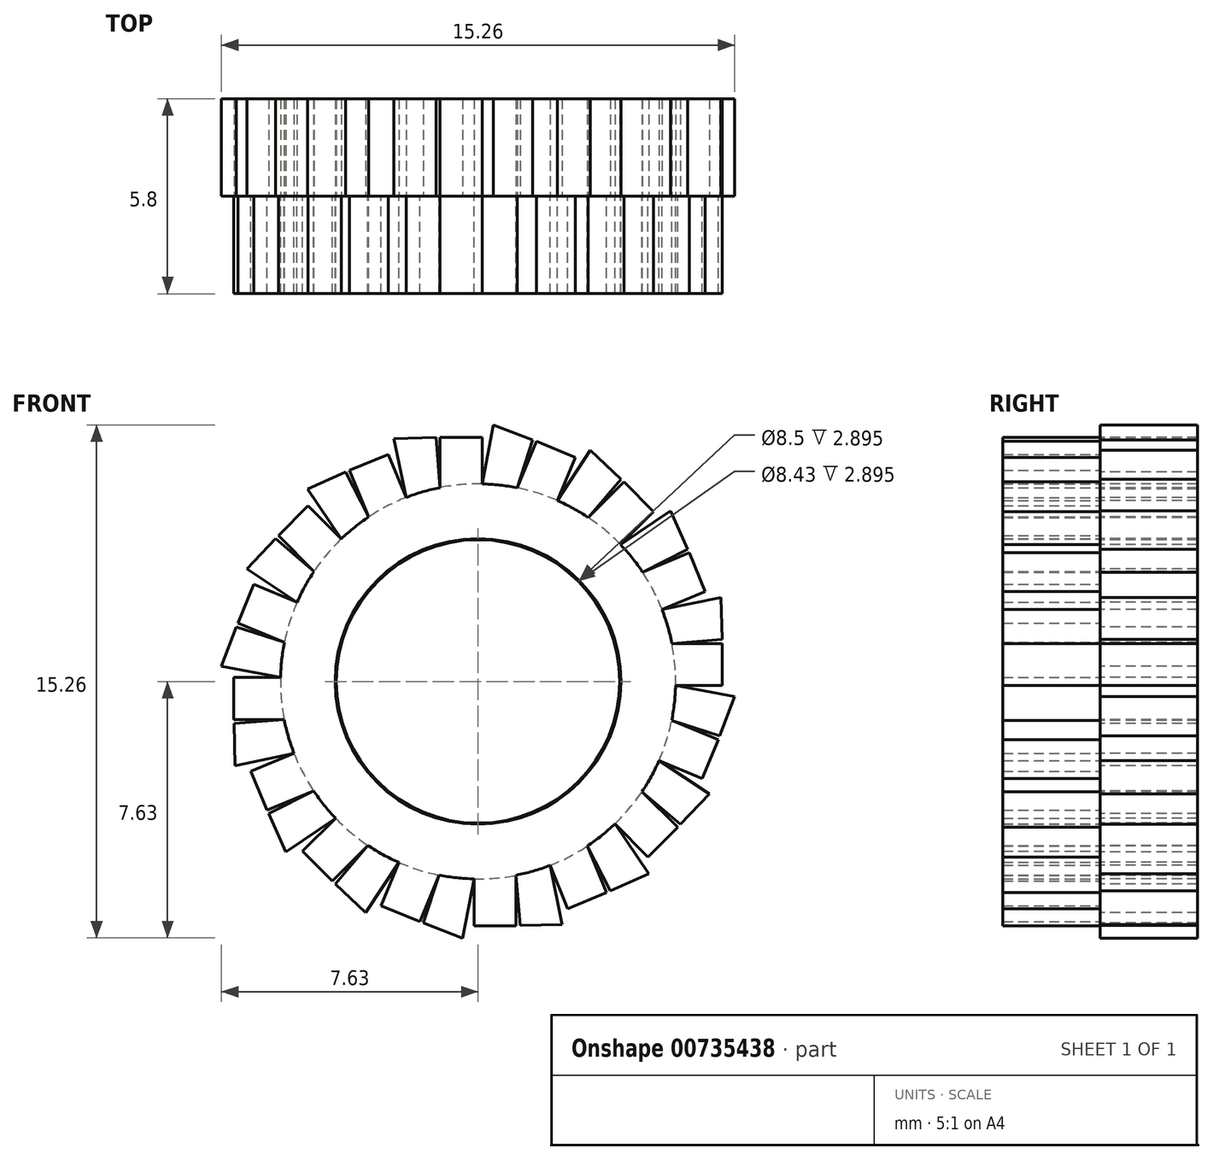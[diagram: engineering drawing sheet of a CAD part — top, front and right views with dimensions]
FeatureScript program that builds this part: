
annotation { "Feature Type Name" : "Feature", "Feature Type Description" : "" }
export const myFeature = defineFeature(function(context is Context, id is Id, definition is map)
    precondition{}
    {
        {
            var Q0;
            Q0=qCreatedBy(makeId("Front.planeOp"),FACE);
            var sketch = newSketch(context, id + "F0", { "sketchPlane" : qUnion([Q0])});
            skCircle(sketch, "E0", {"center": v(0, 0) * mm, "radius": 4.25 * mm});
            skCircle(sketch, "E1", {"center": v(0, 0) * mm, "radius": 5.88 * mm});
            skLineSegment(sketch, "E2", {"start": v(-1.13, 5.77) * mm, "end": v(-1.13, 7.27) * mm});
            skLineSegment(sketch, "E3", {"start": v(-1.13, 7.27) * mm, "end": v(0.12, 7.27) * mm});
            skLineSegment(sketch, "E4", {"start": v(0.12, 7.27) * mm, "end": v(0.12, 5.87) * mm});
            skLineSegment(sketch, "E5.1.0", {"start": v(-3.25, 4.9) * mm, "end": v(-3.83, 6.28) * mm});
            skLineSegment(sketch, "E5.1.1", {"start": v(-3.83, 6.28) * mm, "end": v(-2.67, 6.76) * mm});
            skLineSegment(sketch, "E5.1.2", {"start": v(-2.67, 6.76) * mm, "end": v(-2.14, 5.47) * mm});
            skLineSegment(sketch, "E5.2.0", {"start": v(-4.88, 3.28) * mm, "end": v(-5.94, 4.34) * mm});
            skLineSegment(sketch, "E5.2.1", {"start": v(-5.94, 4.34) * mm, "end": v(-5.05, 5.22) * mm});
            skLineSegment(sketch, "E5.2.2", {"start": v(-5.05, 5.22) * mm, "end": v(-4.07, 4.24) * mm});
            skLineSegment(sketch, "E5.3.0", {"start": v(-5.76, 1.16) * mm, "end": v(-7.14, 1.73) * mm});
            skLineSegment(sketch, "E5.3.1", {"start": v(-7.14, 1.73) * mm, "end": v(-6.67, 2.89) * mm});
            skLineSegment(sketch, "E5.3.2", {"start": v(-6.67, 2.89) * mm, "end": v(-5.38, 2.36) * mm});
            skLineSegment(sketch, "E5.4.0", {"start": v(-5.77, -1.13) * mm, "end": v(-7.27, -1.13) * mm});
            skLineSegment(sketch, "E5.4.1", {"start": v(-7.27, -1.13) * mm, "end": v(-7.27, 0.12) * mm});
            skLineSegment(sketch, "E5.4.2", {"start": v(-7.27, 0.12) * mm, "end": v(-5.87, 0.12) * mm});
            skLineSegment(sketch, "E5.5.0", {"start": v(-4.9, -3.25) * mm, "end": v(-6.28, -3.83) * mm});
            skLineSegment(sketch, "E5.5.1", {"start": v(-6.28, -3.83) * mm, "end": v(-6.76, -2.67) * mm});
            skLineSegment(sketch, "E5.5.2", {"start": v(-6.76, -2.67) * mm, "end": v(-5.47, -2.14) * mm});
            skLineSegment(sketch, "E5.6.0", {"start": v(-3.28, -4.88) * mm, "end": v(-4.34, -5.94) * mm});
            skLineSegment(sketch, "E5.6.1", {"start": v(-4.34, -5.94) * mm, "end": v(-5.22, -5.05) * mm});
            skLineSegment(sketch, "E5.6.2", {"start": v(-5.22, -5.05) * mm, "end": v(-4.24, -4.07) * mm});
            skLineSegment(sketch, "E5.7.0", {"start": v(-1.16, -5.76) * mm, "end": v(-1.73, -7.14) * mm});
            skLineSegment(sketch, "E5.7.1", {"start": v(-1.73, -7.14) * mm, "end": v(-2.89, -6.67) * mm});
            skLineSegment(sketch, "E5.7.2", {"start": v(-2.89, -6.67) * mm, "end": v(-2.36, -5.38) * mm});
            skLineSegment(sketch, "E5.8.0", {"start": v(1.13, -5.77) * mm, "end": v(1.13, -7.27) * mm});
            skLineSegment(sketch, "E5.8.1", {"start": v(1.13, -7.27) * mm, "end": v(-0.12, -7.27) * mm});
            skLineSegment(sketch, "E5.8.2", {"start": v(-0.12, -7.27) * mm, "end": v(-0.12, -5.87) * mm});
            skLineSegment(sketch, "E5.9.0", {"start": v(3.25, -4.9) * mm, "end": v(3.83, -6.28) * mm});
            skLineSegment(sketch, "E5.9.1", {"start": v(3.83, -6.28) * mm, "end": v(2.67, -6.76) * mm});
            skLineSegment(sketch, "E5.9.2", {"start": v(2.67, -6.76) * mm, "end": v(2.14, -5.47) * mm});
            skLineSegment(sketch, "E5.10.0", {"start": v(4.88, -3.28) * mm, "end": v(5.94, -4.34) * mm});
            skLineSegment(sketch, "E5.10.1", {"start": v(5.94, -4.34) * mm, "end": v(5.05, -5.22) * mm});
            skLineSegment(sketch, "E5.10.2", {"start": v(5.05, -5.22) * mm, "end": v(4.07, -4.24) * mm});
            skLineSegment(sketch, "E5.11.0", {"start": v(5.76, -1.16) * mm, "end": v(7.14, -1.73) * mm});
            skLineSegment(sketch, "E5.11.1", {"start": v(7.14, -1.73) * mm, "end": v(6.67, -2.89) * mm});
            skLineSegment(sketch, "E5.11.2", {"start": v(6.67, -2.89) * mm, "end": v(5.38, -2.36) * mm});
            skLineSegment(sketch, "E5.12.0", {"start": v(5.77, 1.13) * mm, "end": v(7.27, 1.13) * mm});
            skLineSegment(sketch, "E5.12.1", {"start": v(7.27, 1.13) * mm, "end": v(7.27, -0.12) * mm});
            skLineSegment(sketch, "E5.12.2", {"start": v(7.27, -0.12) * mm, "end": v(5.87, -0.12) * mm});
            skLineSegment(sketch, "E5.13.0", {"start": v(4.9, 3.25) * mm, "end": v(6.28, 3.83) * mm});
            skLineSegment(sketch, "E5.13.1", {"start": v(6.28, 3.83) * mm, "end": v(6.76, 2.67) * mm});
            skLineSegment(sketch, "E5.13.2", {"start": v(6.76, 2.67) * mm, "end": v(5.47, 2.14) * mm});
            skLineSegment(sketch, "E5.14.0", {"start": v(3.28, 4.88) * mm, "end": v(4.34, 5.94) * mm});
            skLineSegment(sketch, "E5.14.1", {"start": v(4.34, 5.94) * mm, "end": v(5.22, 5.05) * mm});
            skLineSegment(sketch, "E5.14.2", {"start": v(5.22, 5.05) * mm, "end": v(4.24, 4.07) * mm});
            skLineSegment(sketch, "E5.15.0", {"start": v(1.16, 5.76) * mm, "end": v(1.73, 7.14) * mm});
            skLineSegment(sketch, "E5.15.1", {"start": v(1.73, 7.14) * mm, "end": v(2.89, 6.67) * mm});
            skLineSegment(sketch, "E5.15.2", {"start": v(2.89, 6.67) * mm, "end": v(2.36, 5.38) * mm});
            skSolve(sketch);
        }
        {
            var Q0;
            Q0=qSketchRegion(id+"F0",true);
            extrude(context, id + "F1", {"entities" : qUnion([Q0]), "depth" : 2.9 * mm, "offsetDistance" : 25 * mm});
        }
        {
            var Q0;
            Q0=qSketchRegion(id+"F0",true);
            extrude(context, id + "F2", {"entities" : qUnion([Q0]), "operationType" : NewBodyOperationType.ADD, "depth" : 2.9 * mm, "offsetDistance" : 25 * mm});
        }
        {
            var Q0;
            Q0=qSketchRegion(id+"F0",true);
            extrude(context, id + "F3", {"entities" : qUnion([Q0]), "operationType" : NewBodyOperationType.ADD, "depth" : 2.9 * mm, "offsetDistance" : 25 * mm});
        }
        {
            var Q0;
            Q0=makeQuery(id+"F1.opExtrude","CAP_FACE",FACE,{"disambiguationData":[OSD([sQuery(id+"F0.wireOp",EDGE,"E0"),sQuery(id+"F0.wireOp",EDGE,"E1"),sQuery(id+"F0.wireOp",EDGE,"E2"),sQuery(id+"F0.wireOp",EDGE,"E3"),sQuery(id+"F0.wireOp",EDGE,"E4"),sQuery(id+"F0.wireOp",EDGE,"E5.1.0"),sQuery(id+"F0.wireOp",EDGE,"E5.1.1"),sQuery(id+"F0.wireOp",EDGE,"E5.1.2"),sQuery(id+"F0.wireOp",EDGE,"E5.2.0"),sQuery(id+"F0.wireOp",EDGE,"E5.2.1"),sQuery(id+"F0.wireOp",EDGE,"E5.2.2"),sQuery(id+"F0.wireOp",EDGE,"E5.3.0"),sQuery(id+"F0.wireOp",EDGE,"E5.3.1"),sQuery(id+"F0.wireOp",EDGE,"E5.3.2"),sQuery(id+"F0.wireOp",EDGE,"E5.4.0"),sQuery(id+"F0.wireOp",EDGE,"E5.4.1"),sQuery(id+"F0.wireOp",EDGE,"E5.4.2"),sQuery(id+"F0.wireOp",EDGE,"E5.5.0"),sQuery(id+"F0.wireOp",EDGE,"E5.5.1"),sQuery(id+"F0.wireOp",EDGE,"E5.5.2"),sQuery(id+"F0.wireOp",EDGE,"E5.6.0"),sQuery(id+"F0.wireOp",EDGE,"E5.6.1"),sQuery(id+"F0.wireOp",EDGE,"E5.6.2"),sQuery(id+"F0.wireOp",EDGE,"E5.7.0"),sQuery(id+"F0.wireOp",EDGE,"E5.7.1"),sQuery(id+"F0.wireOp",EDGE,"E5.7.2"),sQuery(id+"F0.wireOp",EDGE,"E5.8.0"),sQuery(id+"F0.wireOp",EDGE,"E5.8.1"),sQuery(id+"F0.wireOp",EDGE,"E5.8.2"),sQuery(id+"F0.wireOp",EDGE,"E5.9.0"),sQuery(id+"F0.wireOp",EDGE,"E5.9.1"),sQuery(id+"F0.wireOp",EDGE,"E5.9.2"),sQuery(id+"F0.wireOp",EDGE,"E5.10.0"),sQuery(id+"F0.wireOp",EDGE,"E5.10.1"),sQuery(id+"F0.wireOp",EDGE,"E5.10.2"),sQuery(id+"F0.wireOp",EDGE,"E5.11.0"),sQuery(id+"F0.wireOp",EDGE,"E5.11.1"),sQuery(id+"F0.wireOp",EDGE,"E5.11.2"),sQuery(id+"F0.wireOp",EDGE,"E5.12.0"),sQuery(id+"F0.wireOp",EDGE,"E5.12.1"),sQuery(id+"F0.wireOp",EDGE,"E5.12.2"),sQuery(id+"F0.wireOp",EDGE,"E5.13.0"),sQuery(id+"F0.wireOp",EDGE,"E5.13.1"),sQuery(id+"F0.wireOp",EDGE,"E5.13.2"),sQuery(id+"F0.wireOp",EDGE,"E5.14.0"),sQuery(id+"F0.wireOp",EDGE,"E5.14.1"),sQuery(id+"F0.wireOp",EDGE,"E5.14.2"),sQuery(id+"F0.wireOp",EDGE,"E5.15.0"),sQuery(id+"F0.wireOp",EDGE,"E5.15.1"),sQuery(id+"F0.wireOp",EDGE,"E5.15.2")])],"isStart":true});
            var sketch = newSketch(context, id + "F4", { "sketchPlane" : qUnion([Q0])});
            skPoint(sketch, "E6.start.orphan", {"position": v(0, 8.1) * mm});
            skPoint(sketch, "E7.end.orphan", {"position": v(0, 9.7) * mm});
            skPoint(sketch, "E8.start.orphan", {"position": v(-1.16, 7.14) * mm});
            skPoint(sketch, "E9.endSnap0", {"position": v(-1.45, 6.45) * mm});
            skPoint(sketch, "E10.end.orphan", {"position": v(-0.12, 8.13) * mm});
            skPoint(sketch, "E11.end.orphan", {"position": v(-0.12, 5.87) * mm});
            skPoint(sketch, "E11.start.orphan", {"position": v(-0.68, 7.27) * mm});
            skPoint(sketch, "E12.end.orphan", {"position": v(0, 8.97) * mm});
            skPoint(sketch, "E9.end.orphan", {"position": v(-1.45, 7.95) * mm});
            skCircle(sketch, "E13", {"center": v(0, 0) * mm, "radius": 4.21 * mm});
            skCircle(sketch, "E14", {"center": v(0, 0) * mm, "radius": 5.88 * mm});
            skPoint(sketch, "E15.endSnap0", {"position": v(4.73, -4.56) * mm});
            skPoint(sketch, "E16.start.orphan", {"position": v(6.38, -5.05) * mm});
            skPoint(sketch, "E15.end.orphan", {"position": v(6.73, -4.56) * mm});
            skPoint(sketch, "E17.start.orphan", {"position": v(5.59, 6.28) * mm});
            skLineSegment(sketch, "E18", {"start": v(4.88, 3.28) * mm, "end": v(6.02, 4.25) * mm});
            skPoint(sketch, "E19.end.orphan", {"position": v(7.63, 3.28) * mm});
            skLineSegment(sketch, "E20", {"start": v(5.38, 2.36) * mm, "end": v(6.88, 3.34) * mm});
            skLineSegment(sketch, "E21", {"start": v(6.88, 3.34) * mm, "end": v(6.02, 4.25) * mm});
            skLineSegment(sketch, "E22.1.0", {"start": v(3.25, 4.9) * mm, "end": v(3.93, 6.23) * mm});
            skLineSegment(sketch, "E22.1.1", {"start": v(5.08, 5.72) * mm, "end": v(3.93, 6.23) * mm});
            skLineSegment(sketch, "E22.1.2", {"start": v(4.07, 4.24) * mm, "end": v(5.08, 5.72) * mm});
            skLineSegment(sketch, "E22.2.0", {"start": v(1.13, 5.77) * mm, "end": v(1.25, 7.26) * mm});
            skLineSegment(sketch, "E22.2.1", {"start": v(2.5, 7.23) * mm, "end": v(1.25, 7.26) * mm});
            skLineSegment(sketch, "E22.2.2", {"start": v(2.14, 5.47) * mm, "end": v(2.5, 7.23) * mm});
            skLineSegment(sketch, "E22.3.0", {"start": v(-1.16, 5.76) * mm, "end": v(-1.62, 7.19) * mm});
            skLineSegment(sketch, "E22.3.1", {"start": v(-0.45, 7.63) * mm, "end": v(-1.62, 7.19) * mm});
            skLineSegment(sketch, "E22.3.2", {"start": v(-0.12, 5.87) * mm, "end": v(-0.45, 7.63) * mm});
            skLineSegment(sketch, "E22.4.0", {"start": v(-3.28, 4.88) * mm, "end": v(-4.25, 6.02) * mm});
            skLineSegment(sketch, "E22.4.1", {"start": v(-3.34, 6.88) * mm, "end": v(-4.25, 6.02) * mm});
            skLineSegment(sketch, "E22.4.2", {"start": v(-2.36, 5.38) * mm, "end": v(-3.34, 6.88) * mm});
            skLineSegment(sketch, "E22.5.0", {"start": v(-4.9, 3.25) * mm, "end": v(-6.23, 3.93) * mm});
            skLineSegment(sketch, "E22.5.1", {"start": v(-5.72, 5.08) * mm, "end": v(-6.23, 3.93) * mm});
            skLineSegment(sketch, "E22.5.2", {"start": v(-4.24, 4.07) * mm, "end": v(-5.72, 5.08) * mm});
            skLineSegment(sketch, "E22.6.0", {"start": v(-5.77, 1.13) * mm, "end": v(-7.26, 1.25) * mm});
            skLineSegment(sketch, "E22.6.1", {"start": v(-7.23, 2.5) * mm, "end": v(-7.26, 1.25) * mm});
            skLineSegment(sketch, "E22.6.2", {"start": v(-5.47, 2.14) * mm, "end": v(-7.23, 2.5) * mm});
            skLineSegment(sketch, "E22.7.0", {"start": v(-5.76, -1.16) * mm, "end": v(-7.19, -1.62) * mm});
            skLineSegment(sketch, "E22.7.1", {"start": v(-7.63, -0.45) * mm, "end": v(-7.19, -1.62) * mm});
            skLineSegment(sketch, "E22.7.2", {"start": v(-5.87, -0.12) * mm, "end": v(-7.63, -0.45) * mm});
            skLineSegment(sketch, "E22.8.0", {"start": v(-4.88, -3.28) * mm, "end": v(-6.02, -4.25) * mm});
            skLineSegment(sketch, "E22.8.1", {"start": v(-6.88, -3.34) * mm, "end": v(-6.02, -4.25) * mm});
            skLineSegment(sketch, "E22.8.2", {"start": v(-5.38, -2.36) * mm, "end": v(-6.88, -3.34) * mm});
            skLineSegment(sketch, "E22.9.0", {"start": v(-3.25, -4.9) * mm, "end": v(-3.93, -6.23) * mm});
            skLineSegment(sketch, "E22.9.1", {"start": v(-5.08, -5.72) * mm, "end": v(-3.93, -6.23) * mm});
            skLineSegment(sketch, "E22.9.2", {"start": v(-4.07, -4.24) * mm, "end": v(-5.08, -5.72) * mm});
            skLineSegment(sketch, "E22.10.0", {"start": v(-1.13, -5.77) * mm, "end": v(-1.25, -7.26) * mm});
            skLineSegment(sketch, "E22.10.1", {"start": v(-2.5, -7.23) * mm, "end": v(-1.25, -7.26) * mm});
            skLineSegment(sketch, "E22.10.2", {"start": v(-2.14, -5.47) * mm, "end": v(-2.5, -7.23) * mm});
            skLineSegment(sketch, "E22.11.0", {"start": v(1.16, -5.76) * mm, "end": v(1.62, -7.19) * mm});
            skLineSegment(sketch, "E22.11.1", {"start": v(0.45, -7.63) * mm, "end": v(1.62, -7.19) * mm});
            skLineSegment(sketch, "E22.11.2", {"start": v(0.12, -5.87) * mm, "end": v(0.45, -7.63) * mm});
            skLineSegment(sketch, "E22.12.0", {"start": v(3.28, -4.88) * mm, "end": v(4.25, -6.02) * mm});
            skLineSegment(sketch, "E22.12.1", {"start": v(3.34, -6.88) * mm, "end": v(4.25, -6.02) * mm});
            skLineSegment(sketch, "E22.12.2", {"start": v(2.36, -5.38) * mm, "end": v(3.34, -6.88) * mm});
            skLineSegment(sketch, "E22.13.0", {"start": v(4.9, -3.25) * mm, "end": v(6.23, -3.93) * mm});
            skLineSegment(sketch, "E22.13.1", {"start": v(5.72, -5.08) * mm, "end": v(6.23, -3.93) * mm});
            skLineSegment(sketch, "E22.13.2", {"start": v(4.24, -4.07) * mm, "end": v(5.72, -5.08) * mm});
            skLineSegment(sketch, "E22.14.0", {"start": v(5.77, -1.13) * mm, "end": v(7.26, -1.25) * mm});
            skLineSegment(sketch, "E22.14.1", {"start": v(7.23, -2.5) * mm, "end": v(7.26, -1.25) * mm});
            skLineSegment(sketch, "E22.14.2", {"start": v(5.47, -2.14) * mm, "end": v(7.23, -2.5) * mm});
            skLineSegment(sketch, "E22.15.0", {"start": v(5.76, 1.16) * mm, "end": v(7.19, 1.62) * mm});
            skLineSegment(sketch, "E22.15.1", {"start": v(7.63, 0.45) * mm, "end": v(7.19, 1.62) * mm});
            skLineSegment(sketch, "E22.15.2", {"start": v(5.87, 0.12) * mm, "end": v(7.63, 0.45) * mm});
            skSolve(sketch);
        }
        {
            var Q0;
            Q0=qSketchRegion(id+"F4",true);
            extrude(context, id + "F5", {"entities" : qUnion([Q0]), "operationType" : NewBodyOperationType.ADD, "depth" : 2.9 * mm, "offsetDistance" : 25 * mm});
        }
    });
